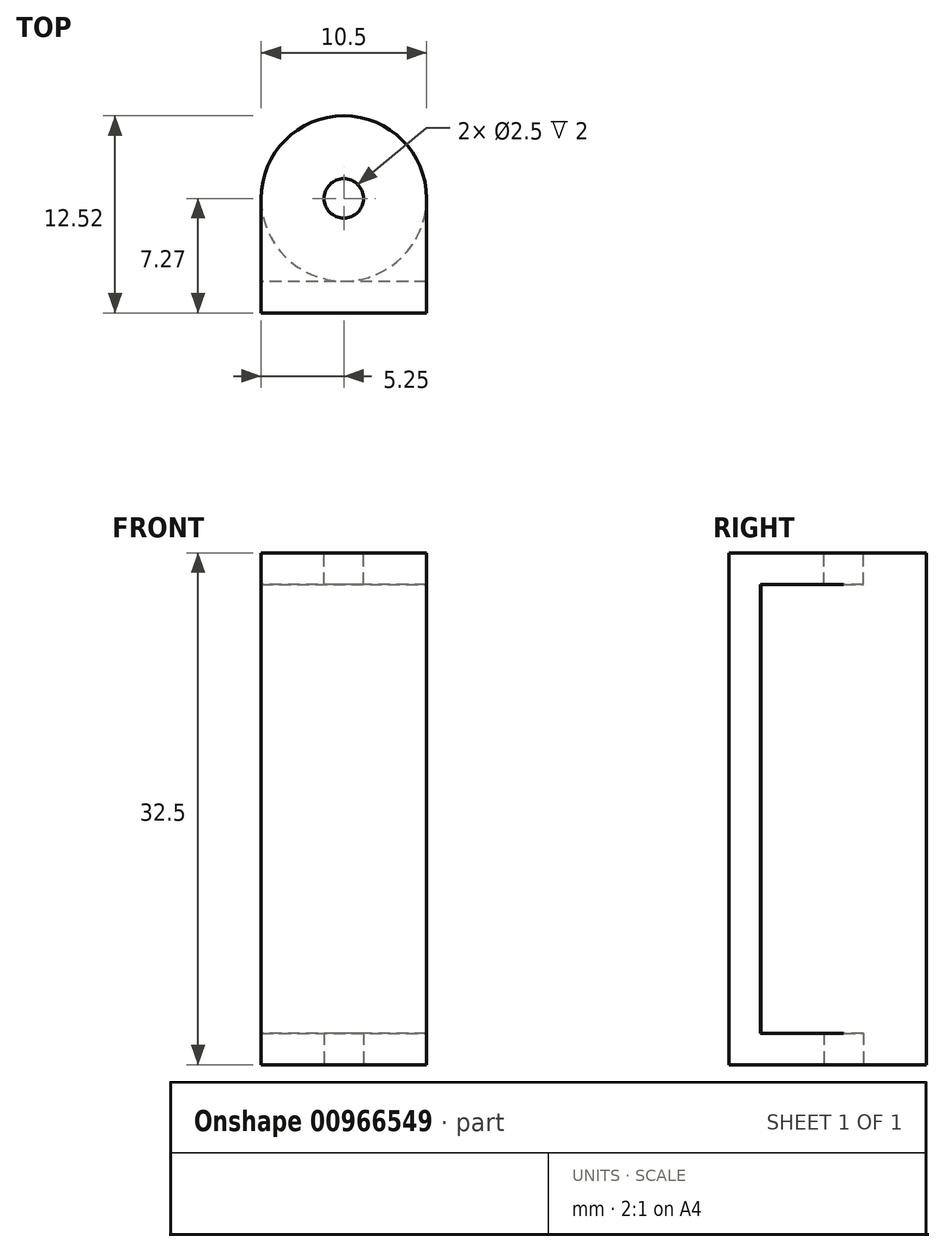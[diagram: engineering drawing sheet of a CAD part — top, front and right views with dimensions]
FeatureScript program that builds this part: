
annotation { "Feature Type Name" : "Feature", "Feature Type Description" : "" }
export const myFeature = defineFeature(function(context is Context, id is Id, definition is map)
    precondition{}
    {
        {
            var Q0;
            Q0=qCreatedBy(makeId("Top.planeOp"),FACE);
            var sketch = newSketch(context, id + "F0", { "sketchPlane" : qUnion([Q0])});
            skCircle(sketch, "E0", {"center": v(0, 0) * mm, "radius": 5.25 * mm});
            skSolve(sketch);
        }
        {
            var Q0;
            Q0 = qSketchRegion(id + "F0", true);
            extrude(context, id + "F1", {"entities" : qUnion([Q0]), "endBound" : BoundingType.SYMMETRIC, "depth" : 28.5 * mm, "offsetDistance" : 25 * mm});
        }
        {
            var Q0;
            Q0=makeQuery(id+"F1.opExtrude","CAP_FACE",FACE,{"disambiguationData":[OSD([sQuery(id+"F0.wireOp",EDGE,"E0")])],"isStart":false});
            var sketch = newSketch(context, id + "F2", { "sketchPlane" : qUnion([Q0])});
            skArc(sketch, "E1.0", {"start": v(5.25, 0) * mm, "mid": v(0, 5.25) * mm, "end": v(-5.25, 0) * mm});
            skLineSegment(sketch, "E2", {"start": v(-5.25, 0) * mm, "end": v(-5.25, -5.27) * mm});
            skLineSegment(sketch, "E3", {"start": v(5.25, 0) * mm, "end": v(5.25, -5.27) * mm});
            skLineSegment(sketch, "E4", {"start": v(5.25, -5.27) * mm, "end": v(-5.25, -5.27) * mm});
            skSolve(sketch);
        }
        {
            var Q0;
            Q0 = qSketchRegion(id + "F2", true);
            extrude(context, id + "F3", {"entities" : qUnion([Q0]), "depth" : 2 * mm, "offsetDistance" : 25 * mm});
        }
        {
            var Q0;
            Q0=makeQuery(id+"F3.opExtrude","CAP_FACE",FACE,{"disambiguationData":[OSD([sQuery(id+"F2.wireOp",EDGE,"E1.0"),sQuery(id+"F2.wireOp",EDGE,"E2"),sQuery(id+"F2.wireOp",EDGE,"E3"),sQuery(id+"F2.wireOp",EDGE,"E4")])],"isStart":false});
            var sketch = newSketch(context, id + "F4", { "sketchPlane" : qUnion([Q0])});
            skLineSegment(sketch, "E5", {"start": v(-5.25, -5.27) * mm, "end": v(-5.25, -7.27) * mm});
            skLineSegment(sketch, "E6", {"start": v(-5.25, -7.27) * mm, "end": v(5.25, -7.27) * mm});
            skLineSegment(sketch, "E7", {"start": v(5.25, -7.27) * mm, "end": v(5.25, -5.27) * mm});
            skSolve(sketch);
        }
        {
            var Q0;
            Q0=makeQuery(id+"F4.imprint","IMPRINT",FACE,{"disambiguationData":[TD([[makeQuery(id+"F4.imprint","IMPRINT",EDGE,{"derivedFrom":sQuery(id+"F4.wireOp",EDGE,"E5")}),1.0]])]});
            var Q1;
            Q1=qCreatedBy(makeId("Top.planeOp"),FACE);
            extrude(context, id + "F5", {"entities" : qUnion([Q0]), "operationType" : NewBodyOperationType.ADD, "endBound" : BoundingType.UP_TO_SURFACE, "oppositeDirection" : true, "depth" : 25 * mm, "endBoundEntityFace" : qUnion([Q1]), "offsetDistance" : 25 * mm});
        }
        {
            var Q0;
            {var subQ0=sQuery(id+"F2.wireOp",EDGE,"E4");Q0=makeQuery(id+"F5.boolean.opBoolean","MERGE",FACE,{"derivedFrom":[makeQuery(id+"F3.opExtrude","CAP_FACE",FACE,{"disambiguationData":[OSD([sQuery(id+"F2.wireOp",EDGE,"E1.0"),sQuery(id+"F2.wireOp",EDGE,"E2"),sQuery(id+"F2.wireOp",EDGE,"E3"),subQ0])],"isStart":false}),makeQuery(id+"F5.opExtrude","CAP_FACE",FACE,{"disambiguationData":[OSD([subQ0,sQuery(id+"F4.wireOp",EDGE,"E5"),sQuery(id+"F4.wireOp",EDGE,"E6"),sQuery(id+"F4.wireOp",EDGE,"E7")])],"isStart":true})]});}
            var sketch = newSketch(context, id + "F6", { "sketchPlane" : qUnion([Q0])});
            skCircle(sketch, "E8", {"center": v(0, 0) * mm, "radius": 1.25 * mm});
            skSolve(sketch);
        }
        {
            var Q0;
            Q0 = qSketchRegion(id + "F6", true);
            extrude(context, id + "F7", {"entities" : qUnion([Q0]), "operationType" : NewBodyOperationType.REMOVE, "endBound" : BoundingType.UP_TO_NEXT, "oppositeDirection" : true, "depth" : 25 * mm, "offsetDistance" : 25 * mm});
        }
        {
            var Q0;
            Q0=makeQuery(id+"F3.opExtrude","SWEPT_BODY",BODY,{"disambiguationData":[OSD([sQuery(id+"F2.wireOp",EDGE,"E1.0"),sQuery(id+"F2.wireOp",EDGE,"E2"),sQuery(id+"F2.wireOp",EDGE,"E3"),sQuery(id+"F2.wireOp",EDGE,"E4")])]});
            var Q1;
            Q1=qCreatedBy(makeId("Top.planeOp"),FACE);
            mirror(context, id + "F8", {"operationType" : NewBodyOperationType.ADD, "entities" : qUnion([Q0]), "mirrorPlane" : qUnion([Q1])});
        }
    });
